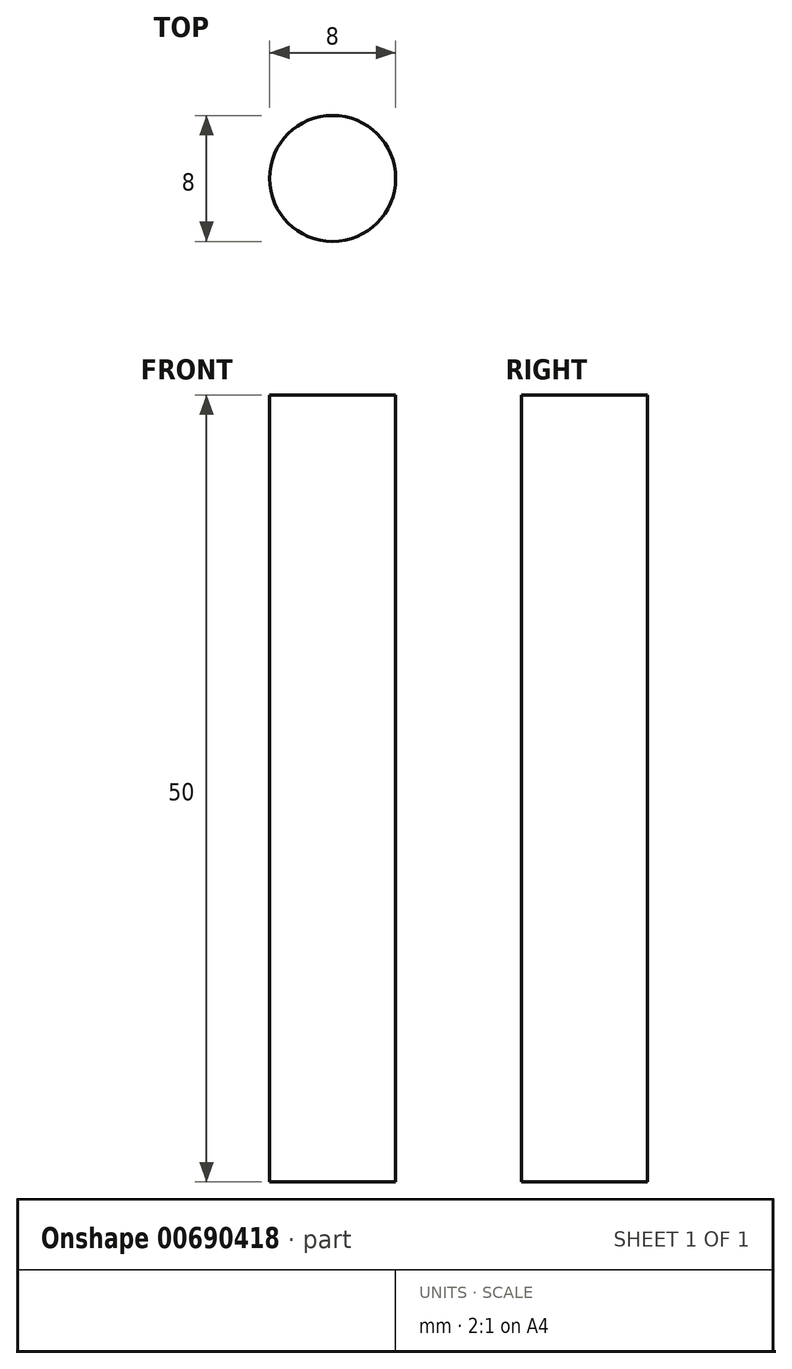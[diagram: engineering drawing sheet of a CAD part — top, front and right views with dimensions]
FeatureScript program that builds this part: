
annotation { "Feature Type Name" : "Feature", "Feature Type Description" : "" }
export const myFeature = defineFeature(function(context is Context, id is Id, definition is map)
    precondition{}
    {
        {
            var Q0;
            Q0=qCreatedBy(makeId("Top.planeOp"),FACE);
            var sketch = newSketch(context, id + "F0", { "sketchPlane" : qUnion([Q0])});
            skCircle(sketch, "E0", {"center": v(0, 0.25) * mm, "radius": 4 * mm});
            skSolve(sketch);
        }
        {
            var Q0;
            Q0=makeQuery(id+"F0.imprint","IMPRINT",FACE,{"disambiguationData":[TD([[makeQuery(id+"F0.imprint","IMPRINT",EDGE,{"derivedFrom":sQuery(id+"F0.wireOp",EDGE,"E0")}),1.0]])]});
            extrude(context, id + "F1", {"entities" : qUnion([Q0]), "depth" : 50 * mm, "offsetDistance" : 25 * mm});
        }
    });
